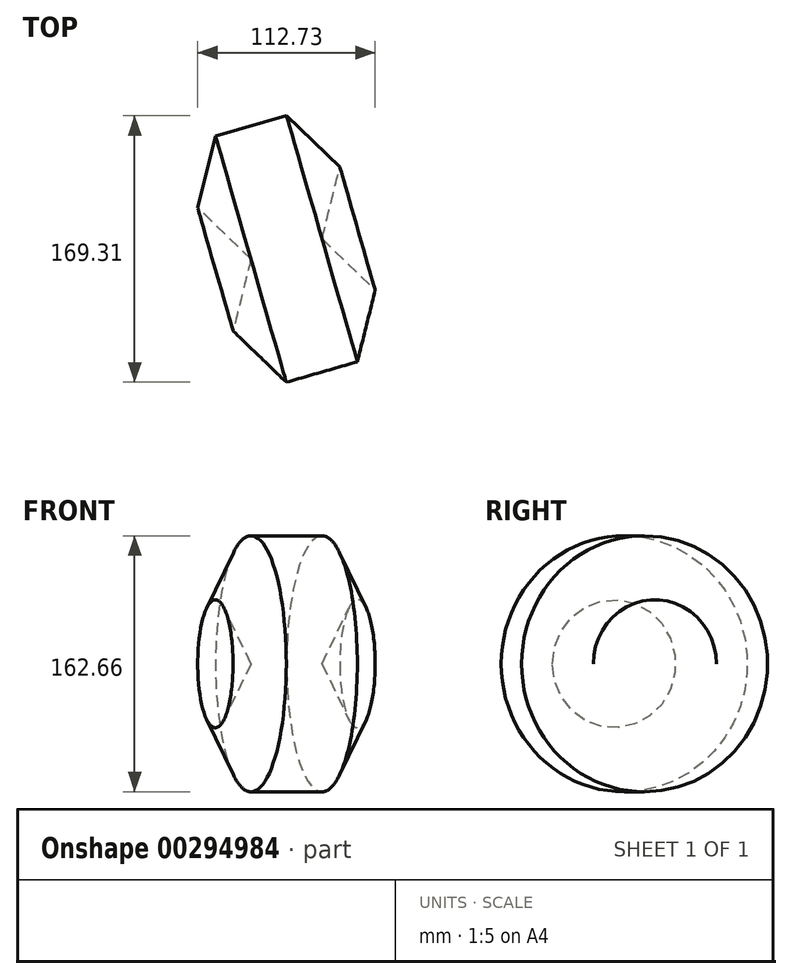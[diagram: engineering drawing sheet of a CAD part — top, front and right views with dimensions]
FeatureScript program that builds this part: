
annotation { "Feature Type Name" : "Feature", "Feature Type Description" : "" }
export const myFeature = defineFeature(function(context is Context, id is Id, definition is map)
    precondition{}
    {
        {
            var Q0;
            Q0=qCreatedBy(makeId("Top.planeOp"),FACE);
            var sketch = newSketch(context, id + "F0", { "sketchPlane" : qUnion([Q0])});
            skCircle(sketch, "E0.cCircle", {"center": v(2.6, 3.31) * mm, "radius": 40.67 * mm, "construction": true});
            skLineSegment(sketch, "E0.0", {"start": v(13.92, 48.88) * mm, "end": v(47.72, 16.28) * mm});
            skLineSegment(sketch, "E0.1", {"start": v(47.72, 16.28) * mm, "end": v(36.39, -29.29) * mm});
            skLineSegment(sketch, "E0.2", {"start": v(36.39, -29.29) * mm, "end": v(-8.74, -42.26) * mm});
            skLineSegment(sketch, "E0.3", {"start": v(-8.74, -42.26) * mm, "end": v(-42.54, -9.66) * mm});
            skLineSegment(sketch, "E0.4", {"start": v(-42.54, -9.66) * mm, "end": v(-31.2, 35.9) * mm});
            skLineSegment(sketch, "E0.5", {"start": v(-31.2, 35.9) * mm, "end": v(13.92, 48.88) * mm});
            skPoint(sketch, "E0.0.midPoint", {"position": v(30.82, 32.58) * mm});
            skSolve(sketch);
        }
        {
            var Q0;
            Q0=makeQuery(id+"F0.imprint","IMPRINT",FACE,{"disambiguationData":[TD([[makeQuery(id+"F0.imprint","IMPRINT",EDGE,{"derivedFrom":sQuery(id+"F0.wireOp",EDGE,"E0.0")}),-1.0]])]});
            var Q1;
            Q1=sQuery(id+"F0.wireOp",EDGE,"E0.5");
            revolve(context, id + "F1", {"entities" : qUnion([Q0]), "axis" : qUnion([Q1]), "revolveType" : RevolveType.FULL});
        }
    });
